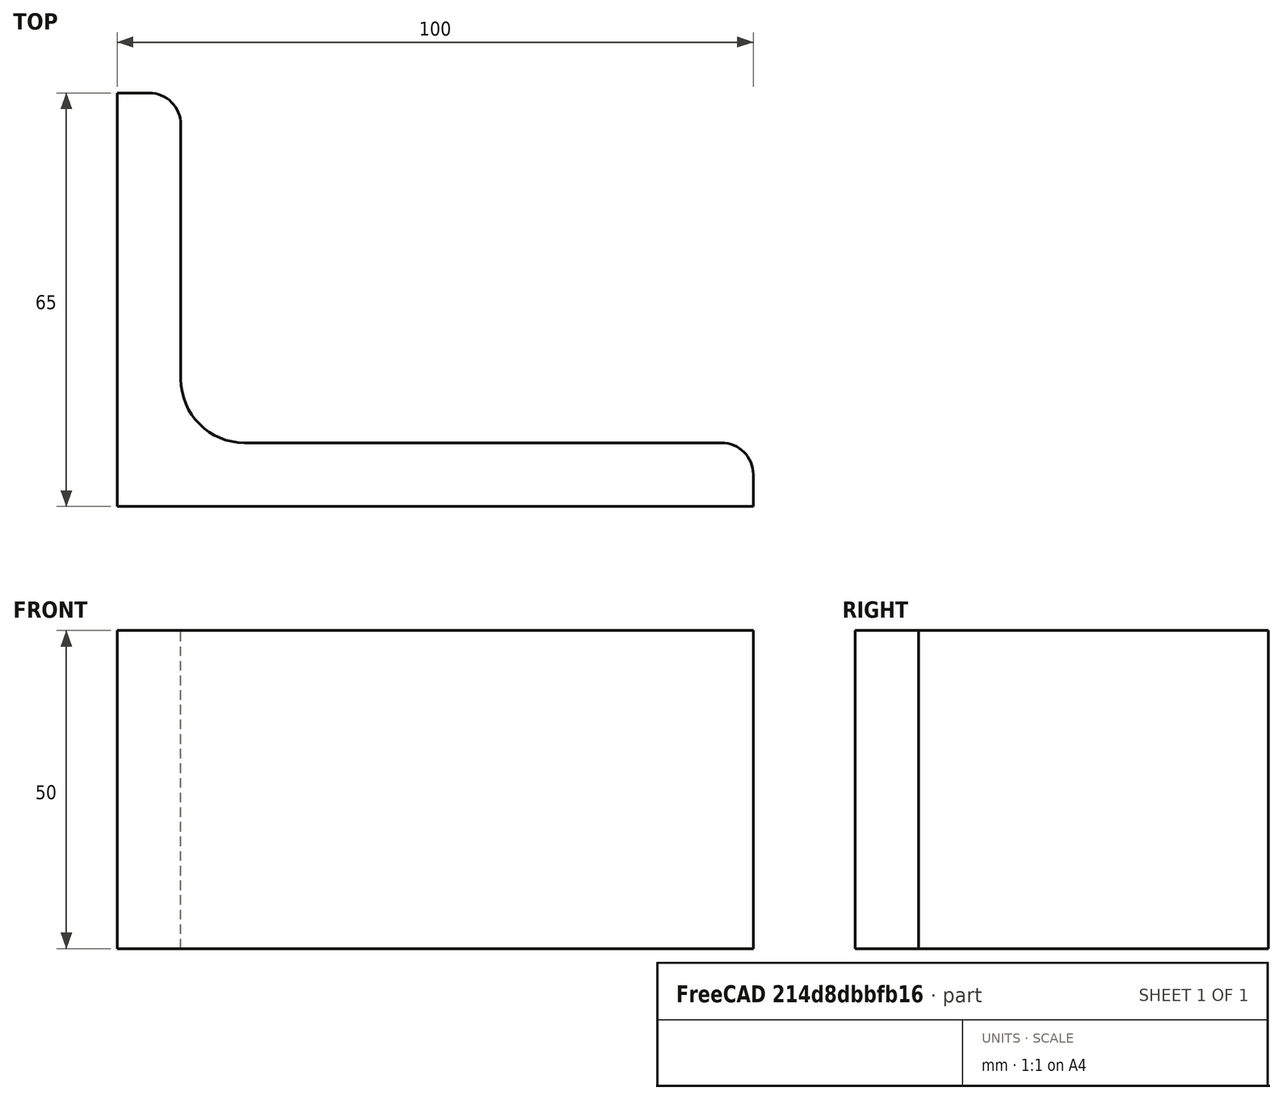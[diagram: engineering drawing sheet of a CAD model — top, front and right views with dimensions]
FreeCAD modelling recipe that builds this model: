
FCSTD DOCUMENT  (FreeCAD 0.15R4671 (Git))
Label: Angle Bar 100x65x10 EN10056 S235JR
License: All rights reserved
LicenseURL: http://en.wikipedia.org/wiki/All_rights_reserved
objects: Sketcher::SketchObject×1, Part::Extrusion×1
note: 2 computed .brp shape members not serialized (recipe doc carries the construction recipe); baked Part::Feature solids carry a one-line shape summary decoded from their .brp

FEATURE [Sketcher::SketchObject] Sketch
  sketch-geometry (9):
    g0: LineSegment StartX=0 StartY=0 StartZ=0 EndX=100 EndY=0 EndZ=0
    g1: LineSegment StartX=100 StartY=0 StartZ=0 EndX=100 EndY=5 EndZ=0
    g2: LineSegment StartX=95 StartY=10 StartZ=0 EndX=20 EndY=10 EndZ=0
    g3: LineSegment StartX=0 StartY=0 StartZ=0 EndX=0 EndY=65 EndZ=0
    g4: LineSegment StartX=0 StartY=65 StartZ=0 EndX=5 EndY=65 EndZ=0
    g5: LineSegment StartX=10 StartY=60 StartZ=0 EndX=10 EndY=20 EndZ=0
    g6: ArcOfCircle CenterX=20 CenterY=20 CenterZ=0 NormalX=0 NormalY=0 NormalZ=1 Radius=10 StartAngle=3.14159 EndAngle=4.71239
    g7: ArcOfCircle CenterX=5 CenterY=60 CenterZ=0 NormalX=0 NormalY=0 NormalZ=1 Radius=5 StartAngle=0 EndAngle=1.5708
    g8: ArcOfCircle CenterX=95 CenterY=5 CenterZ=0 NormalX=0 NormalY=0 NormalZ=1 Radius=5 StartAngle=0 EndAngle=1.5708
  constraints (23):
    c: Coincident(g0,g-1)
    c: Horizontal(g0)
    c: Coincident(g1,g0)
    c: Vertical(g1)
    c: Horizontal(g2)
    c: Coincident(g3,g-1)
    c: Vertical(g3)
    c: Coincident(g4,g3)
    c: Horizontal(g4)
    c: Vertical(g5)
    c: Tangent(g5,g6) = -1.5708
    c: Tangent(g2,g6) = 1.5708
    c: Tangent(g4,g7) = 1.5708
    c: Tangent(g5,g7) = 1.5708
    c: Tangent(g2,g8) = -1.5708
    c: Tangent(g1,g8) = -1.5708
    c: DistanceX(g0) = 100
    c: DistanceY(g3) = 65
    c: DistanceY(g0,g2) = 10
    c: DistanceX(g3,g5) = 10
    c: Radius(g6) = 10
    c: Radius(g8) = 5
    c: Radius(g7) = 5
FEATURE [Part::Extrusion] Extrude  label="Angle Bar 100x65x10 EN10056 S235JR"
  Base = -> Sketch
  Dir = (0,0,50)
  Solid = true
